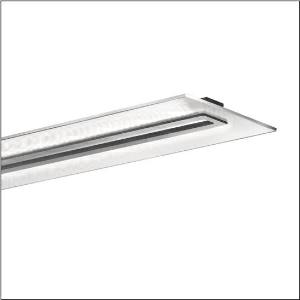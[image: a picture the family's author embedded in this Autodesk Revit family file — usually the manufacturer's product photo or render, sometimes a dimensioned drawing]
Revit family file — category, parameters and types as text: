
# Revit family: vega_r__11_5mn238dlc_e876
name_source: partatom
category: Lighting Fixtures
units: mm (PartAtom-declared; Revit-internal decimal feet)

## family parameters
Cut with Voids When Loaded = No
Host = Face
Light Source = No
Part Type = Normal
Room Calculation Point = No
Round Connector Dimension = Use Diameter
Shared = No

## types (1)
- --- (1 x LED 4000K / CRI = 80 (unbekannt), 4300 lm, 4000K)
    Apparent Load = 31 VA
    CIE Flux Codes = 61 86 97 62 100
    Color Rendering = 80
    Color Temperature = 4000K
    Default Elevation = 1800 mm
    Description = Vega® 11, office luminaire, primary light control with prismatic reflector, of PMMA, transparent prismatic structure, CAT 2 (L<= 1500cd/m²), light emission: direct/indirect distribution, primary light characteristic: symmetric, installation type: suspended mounting, surface-mounted, LED, rated luminous flux: 4.300lm, luminous efficacy: 139lm/W, light colour: 840, colour temperature: 4000K, control gear: ECG, with terminal, 3+2-pole, max. 2.5mm², mains connection: 230V, AC, 50Hz, connection cable inclusive, cable length: 1,5m, rated input power: 31W, luminaire housing, rectangular, rounded, of aluminium section, anodised, metallic grey (RAL 9006), length: 1.250mm, width: 350mm, height: 43mm, luminaire housing, lower part, of aluminium section, anodised, metallic grey (RAL 9006), of PC, grey, protection rating (complete): IP20, insulation class (complete): insulation class I (protective earthing), certification: CE, standard: EN 50419, packaging unit: 1 piece
    Height = 40 mm  [stored 0.131234 ft]
    Lamp = 1 x LED 4000K / CRI >= 80 (unbekannt)
    Lamp Light Flux = 4300 lm
    Lamp count = 1
    Length = 1250 mm
    Luminous efficacy = 139 lm/W
    Manufacturer = Siteco
    ModVariant = No
    Model = 5MN238DLC
    Mounting Place = Ceiling
    Mounting Type = Pendant
    Number of Poles = 1
    OnlyDefault = Yes
    Power Factor = 1
    Product Name = Vega® 11
    Product group = office luminaire | ceiling pendant
    ProductGroupID = 902
    Protection Class = Protection class I
    Protection Degree = IP 20
    RLX_Detail_Level = 1
    RLX_Emergency_Light_Flux = 0 lm
    RLX_Emergency_Type = 0
    RLX_Emergency_Type_DB = No
    RlxData = <blob elided: 62877 chars, md5=2771959f>
    Socket = socket
    Standby Power = 0 W
    System Light Flux = 4300 lm
    System Power = 31 W
    Type Comments = factory setting: luminous flux: 100 % | dim-lin: 254 | 231 mA
    Type Image = l_1004807.jpg
    URL = http://relux.com
    VarID = @adj_165421
    Voltage = 0 V
    Weight = 0.00 kg
    Width = 350 mm

note: [stored X ft] marks values corroborated as IEEE doubles in the binary element streams (Revit-internal decimal feet)

## geometry (parser evidence)
native form markers: Blend x4, Sweep x13
no freeform markers — native parametric forms only
